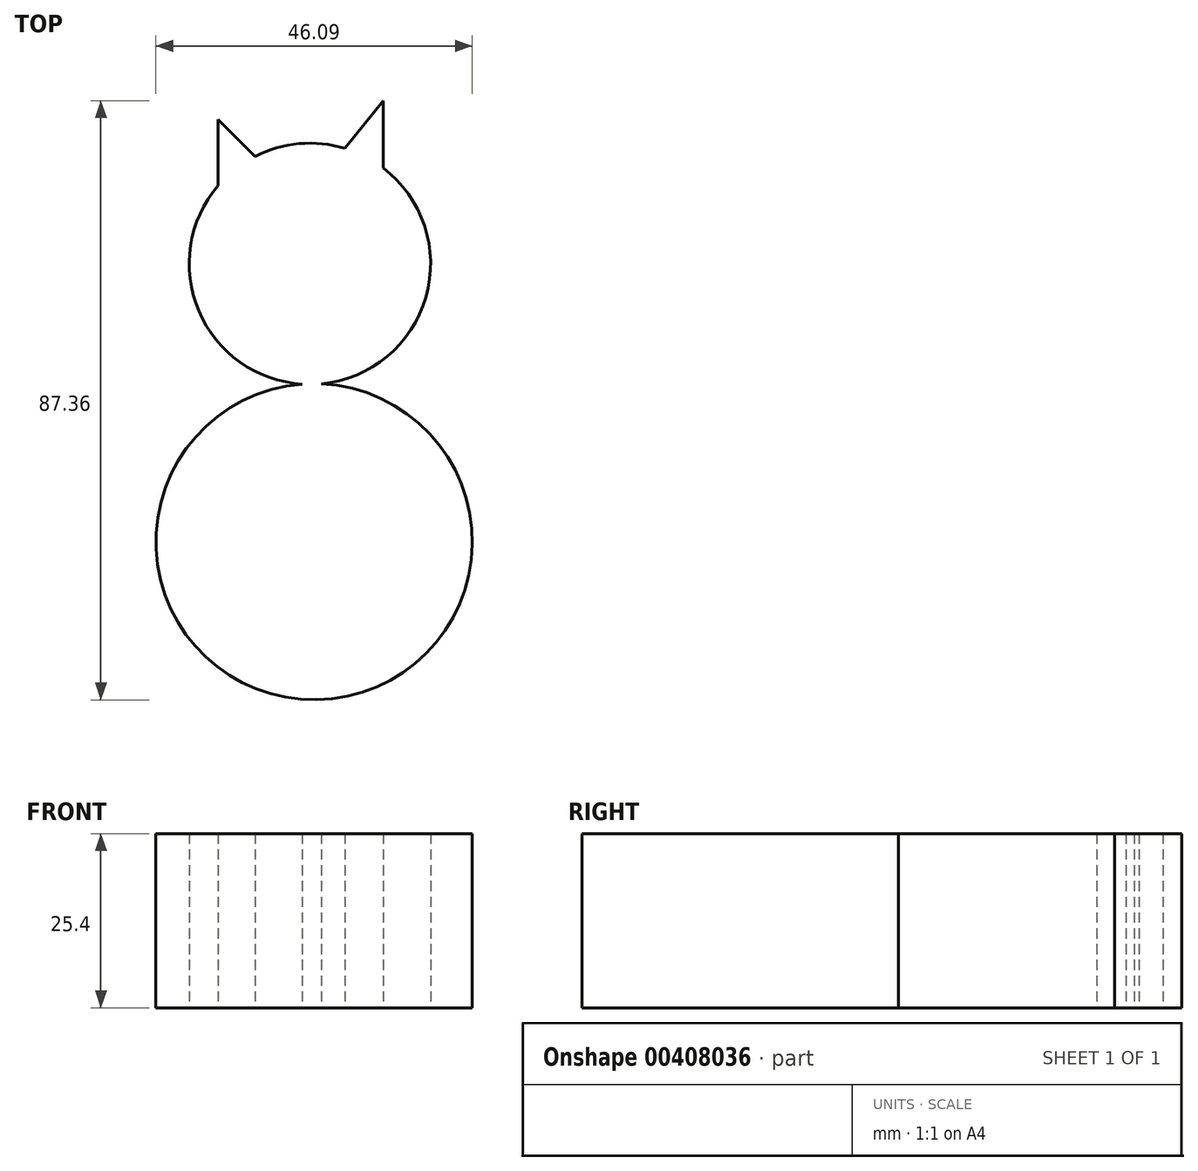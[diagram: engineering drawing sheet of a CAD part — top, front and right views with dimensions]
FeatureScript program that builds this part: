
annotation { "Feature Type Name" : "Feature", "Feature Type Description" : "" }
export const myFeature = defineFeature(function(context is Context, id is Id, definition is map)
    precondition{}
    {
        {
            var Q0;
            Q0=qCreatedBy(makeId("Top.planeOp"),FACE);
            var sketch = newSketch(context, id + "F0", { "sketchPlane" : qUnion([Q0])});
            skCircle(sketch, "E0", {"center": v(-23.78, 49.83) * mm, "radius": 17.59 * mm});
            skLineSegment(sketch, "E1", {"start": v(-37.17, 61.24) * mm, "end": v(-37.17, 70.87) * mm});
            skLineSegment(sketch, "E2", {"start": v(-37.17, 70.87) * mm, "end": v(-31.77, 65.5) * mm});
            skLineSegment(sketch, "E3", {"start": v(-18.67, 66.66) * mm, "end": v(-13.1, 73.6) * mm});
            skLineSegment(sketch, "E4", {"start": v(-13.1, 73.6) * mm, "end": v(-13.1, 63.8) * mm});
            skCircle(sketch, "E5", {"center": v(-23.16, 9.3) * mm, "radius": 23.05 * mm});
            skLineSegment(sketch, "E6", {"start": v(-42.76, 21.43) * mm, "end": v(-50.3, 33.07) * mm});
            skLineSegment(sketch, "E7", {"start": v(-50.3, 33.07) * mm, "end": v(-58.2, 33.28) * mm});
            skLineSegment(sketch, "E8", {"start": v(-50.3, 33.07) * mm, "end": v(-50.3, 40.08) * mm});
            skLineSegment(sketch, "E9", {"start": v(-3.57, 21.43) * mm, "end": v(4.57, 33.07) * mm});
            skLineSegment(sketch, "E10", {"start": v(4.57, 33.07) * mm, "end": v(0, 40.13) * mm});
            skLineSegment(sketch, "E11", {"start": v(4.57, 33.07) * mm, "end": v(12.9, 38.46) * mm});
            skCircle(sketch, "E12", {"center": v(-33.53, 56.85) * mm, "radius": 3.37 * mm});
            skCircle(sketch, "E13", {"center": v(-18.9, 56.85) * mm, "radius": 4.28 * mm});
            skArc(sketch, "E14", {"start": v(-27.74, 43.43) * mm, "mid": v(-20.03, 35.28) * mm, "end": v(-17.37, 46.18) * mm});
            skSolve(sketch);
        }
        {
            var Q0;
            Q0=makeQuery(id+"F0.imprint","IMPRINT",FACE,{"disambiguationData":[TD([[makeQuery(id+"F0.imprint","IMPRINT",EDGE,{"derivedFrom":sQuery(id+"F0.wireOp",EDGE,"E13")}),1.0]])]});
            var Q1;
            Q1=makeQuery(id+"F0.imprint","IMPRINT",FACE,{"disambiguationData":[TD([[makeQuery(id+"F0.imprint","IMPRINT",EDGE,{"derivedFrom":sQuery(id+"F0.wireOp",EDGE,"E12")}),1.0]])]});
            var Q2;
            Q2=makeQuery(id+"F0.imprint","IMPRINT",FACE,{"disambiguationData":[TD([[makeQuery(id+"F0.imprint","IMPRINT",EDGE,{"derivedFrom":sQuery(id+"F0.wireOp",EDGE,"E12")}),-1.0]])]});
            var Q3;
            {var subQ0=sQuery(id+"F0.wireOp",EDGE,"E3");Q3=makeQuery(id+"F0.imprint","IMPRINT",FACE,{"disambiguationData":[TD([[makeQuery(id+"F0.imprint","IMPRINT",EDGE,{"derivedFrom":subQ0}),-1.0]])]});}
            var Q4;
            {var subQ0=sQuery(id+"F0.wireOp",EDGE,"E1");Q4=makeQuery(id+"F0.imprint","IMPRINT",FACE,{"disambiguationData":[TD([[makeQuery(id+"F0.imprint","IMPRINT",EDGE,{"derivedFrom":subQ0}),-1.0]])]});}
            var Q5;
            {var subQ0=sQuery(id+"F0.wireOp",EDGE,"E5");var subQ5=makeQuery(id+"F0.imprint","IMPRINT",VERTEX,{"disambiguationData":[OD(0.0)],"derivedFrom":subQ0});Q5=makeQuery(id+"F0.imprint","IMPRINT",FACE,{"disambiguationData":[TD([[makeQuery(id+"F0.imprint","IMPRINT",EDGE,{"disambiguationData":[TD([[subQ5,-1.0]])],"derivedFrom":subQ0}),1.0]])]});}
            var Q6;
            {var subQ0=sQuery(id+"F0.wireOp",EDGE,"E5");var subQ1=sQuery(id+"F0.wireOp",EDGE,"E0");var subQ2=makeQuery(id+"F0.imprint","INTERSECT",VERTEX,{"disambiguationData":[OD(0.0)],"derivedFrom":[subQ1,subQ0]});Q6=makeQuery(id+"F0.imprint","IMPRINT",FACE,{"disambiguationData":[TD([[makeQuery(id+"F0.imprint","IMPRINT",EDGE,{"disambiguationData":[TD([[subQ2,-1.0]])],"derivedFrom":subQ1}),1.0]])]});}
            extrude(context, id + "F1", {"entities" : qUnion([Q0, Q1, Q2, Q3, Q4, Q5, Q6]), "depth" : 25.4 * mm});
        }
    });
